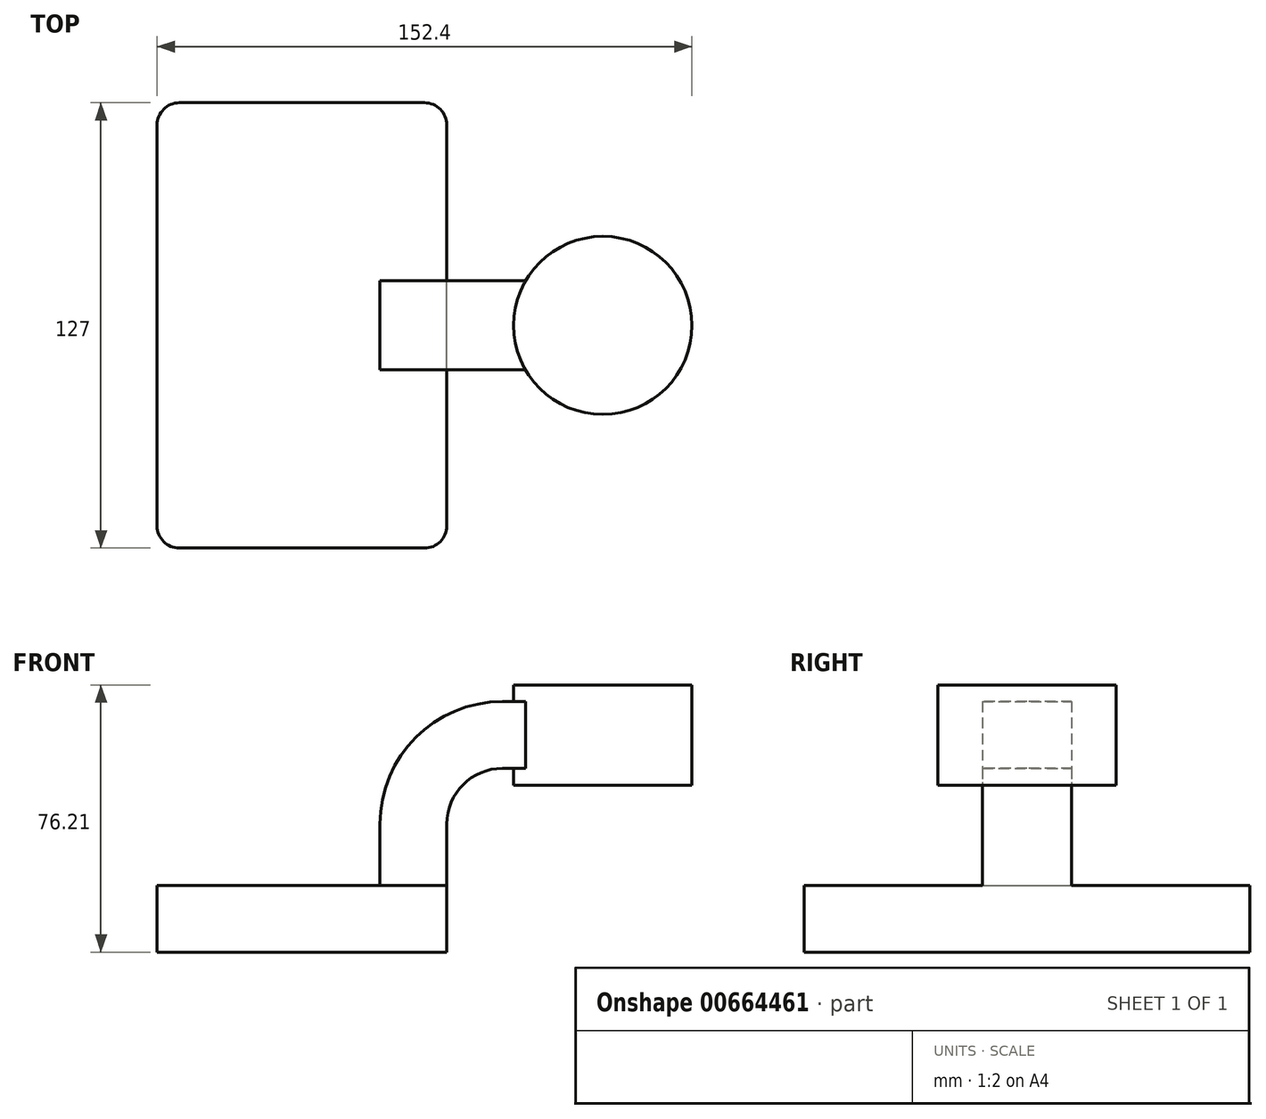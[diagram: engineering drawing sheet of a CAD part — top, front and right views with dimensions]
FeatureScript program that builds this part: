
annotation { "Feature Type Name" : "Feature", "Feature Type Description" : "" }
export const myFeature = defineFeature(function(context is Context, id is Id, definition is map)
    precondition{}
    {
        {
            var Q0;
            Q0=qCreatedBy(makeId("Front.planeOp"),FACE);
            var sketch = newSketch(context, id + "F0", { "sketchPlane" : qUnion([Q0])});
            skLineSegment(sketch, "E0.bottom", {"start": v(41.28, -9.53) * mm, "end": v(-41.28, -9.53) * mm});
            skLineSegment(sketch, "E0.top", {"start": v(41.28, 9.52) * mm, "end": v(-41.28, 9.52) * mm});
            skLineSegment(sketch, "E0.left", {"start": v(41.28, -9.52) * mm, "end": v(41.28, 9.53) * mm});
            skLineSegment(sketch, "E0.right", {"start": v(-41.28, -9.52) * mm, "end": v(-41.28, 9.53) * mm});
            skPoint(sketch, "E0.middle", {"position": v(0, 0) * mm});
            skLineSegment(sketch, "E1.bottom", {"start": v(85.72, 38.1) * mm, "end": v(60.33, 38.1) * mm});
            skLineSegment(sketch, "E1.top", {"start": v(111.12, 66.67) * mm, "end": v(60.33, 66.67) * mm});
            skLineSegment(sketch, "E1.left", {"start": v(111.12, 38.1) * mm, "end": v(111.12, 66.68) * mm});
            skLineSegment(sketch, "E1.right", {"start": v(60.32, 38.1) * mm, "end": v(60.32, 66.68) * mm});
            skPoint(sketch, "E1.middle", {"position": v(85.72, 52.39) * mm});
            skLineSegment(sketch, "E2", {"start": v(41.28, 9.53) * mm, "end": v(41.28, 27) * mm});
            skArc(sketch, "E3", {"start": v(41.27, 27) * mm, "mid": v(45.92, 38.23) * mm, "end": v(57.15, 42.88) * mm});
            skLineSegment(sketch, "E4", {"start": v(57.15, 42.88) * mm, "end": v(85.72, 42.88) * mm});
            skPoint(sketch, "E4.endSnap0", {"position": v(85.72, 38.1) * mm});
            skLineSegment(sketch, "E5", {"start": v(85.72, 38.1) * mm, "end": v(111.12, 38.1) * mm});
            skLineSegment(sketch, "E6.0", {"start": v(57.15, 61.93) * mm, "end": v(85.73, 61.93) * mm});
            skArc(sketch, "E6.1", {"start": v(22.23, 27) * mm, "mid": v(32.45, 51.7) * mm, "end": v(57.15, 61.93) * mm});
            skLineSegment(sketch, "E6.2", {"start": v(22.23, 9.52) * mm, "end": v(22.23, 27) * mm});
            skLineSegment(sketch, "E7", {"start": v(85.72, 38.1) * mm, "end": v(85.72, 66.68) * mm});
            skFitSpline(sketch, "E8", {"points": [v(-41.28, 9.52) * mm, v(57.15, 61.93) * mm], "startDerivative": vector(0, 80.45) * mm, "endDerivative": vector(151.05, 0) * mm});
            skSolve(sketch);
        }
        {
            var Q0;
            Q0=makeQuery(id+"F0.imprint","IMPRINT",FACE,{"disambiguationData":[TD([[makeQuery(id+"F0.imprint","IMPRINT",EDGE,{"derivedFrom":sQuery(id+"F0.wireOp",EDGE,"E0.bottom")}),-1.0]])]});
            extrude(context, id + "F1", {"entities" : qUnion([Q0]), "endBound" : BoundingType.SYMMETRIC, "depth" : 127 * mm});
        }
        {
            var Q0;
            {var subQ1=sQuery(id+"F0.wireOp",EDGE,"E2");Q0=makeQuery(id+"F0.imprint","IMPRINT",FACE,{"disambiguationData":[TD([[makeQuery(id+"F0.imprint","IMPRINT",EDGE,{"derivedFrom":subQ1}),1.0]])]});}
            var Q1;
            {var subQ0=sQuery(id+"F0.wireOp",EDGE,"E4");var subQ1=sQuery(id+"F0.wireOp",EDGE,"E1.right");var subQ2=makeQuery(id+"F0.imprint","INTERSECT",VERTEX,{"derivedFrom":[subQ1,subQ0]});Q1=makeQuery(id+"F0.imprint","IMPRINT",FACE,{"disambiguationData":[TD([[makeQuery(id+"F0.imprint","IMPRINT",EDGE,{"disambiguationData":[TD([[subQ2,-1.0]])],"derivedFrom":subQ1}),-1.0]])]});}
            extrude(context, id + "F2", {"entities" : qUnion([Q0, Q1]), "operationType" : NewBodyOperationType.ADD, "endBound" : BoundingType.SYMMETRIC, "depth" : 25.4 * mm});
        }
        {
            var Q0;
            Q0=makeQuery(id+"F0.imprint","IMPRINT",FACE,{"disambiguationData":[TD([[makeQuery(id+"F0.imprint","IMPRINT",EDGE,{"derivedFrom":sQuery(id+"F0.wireOp",EDGE,"E6.1")}),1.0]])]});
            extrude(context, id + "F3", {"entities" : qUnion([Q0]), "operationType" : NewBodyOperationType.ADD, "endBound" : BoundingType.SYMMETRIC, "depth" : 16.13 * mm});
        }
        {
            var Q0;
            {var subQ0=sQuery(id+"F0.wireOp",EDGE,"E1.left");Q0=makeQuery(id+"F0.imprint","IMPRINT",FACE,{"disambiguationData":[TD([[makeQuery(id+"F0.imprint","IMPRINT",EDGE,{"derivedFrom":subQ0}),1.0]])]});}
            var Q1;
            Q1=sQuery(id+"F0.wireOp",EDGE,"E7");
            revolve(context, id + "F4", {"operationType" : NewBodyOperationType.ADD, "entities" : qUnion([Q0]), "axis" : qUnion([Q1]), "revolveType" : RevolveType.FULL});
        }
        {
            var Q0;
            Q0=makeQuery(id+"F1.opExtrude","CAP_EDGE",EDGE,{"disambiguationData":[OSD([sQuery(id+"F0.wireOp",EDGE,"E0.left")])],"isStart":false});
            var Q1;
            Q1=makeQuery(id+"F1.opExtrude","CAP_EDGE",EDGE,{"disambiguationData":[OSD([sQuery(id+"F0.wireOp",EDGE,"E0.right")])],"isStart":false});
            var Q2;
            Q2=makeQuery(id+"F1.opExtrude","CAP_EDGE",EDGE,{"disambiguationData":[OSD([sQuery(id+"F0.wireOp",EDGE,"E0.right")])],"isStart":true});
            var Q3;
            Q3=makeQuery(id+"F1.opExtrude","CAP_EDGE",EDGE,{"disambiguationData":[OSD([sQuery(id+"F0.wireOp",EDGE,"E0.left")])],"isStart":true});
            fillet(context, id + "F5", {"entities" : qUnion([Q0, Q1, Q2, Q3]), "radius" : 6.35 * mm, "tangentPropagation" : true, "allowEdgeOverflow" : false});
        }
    });
